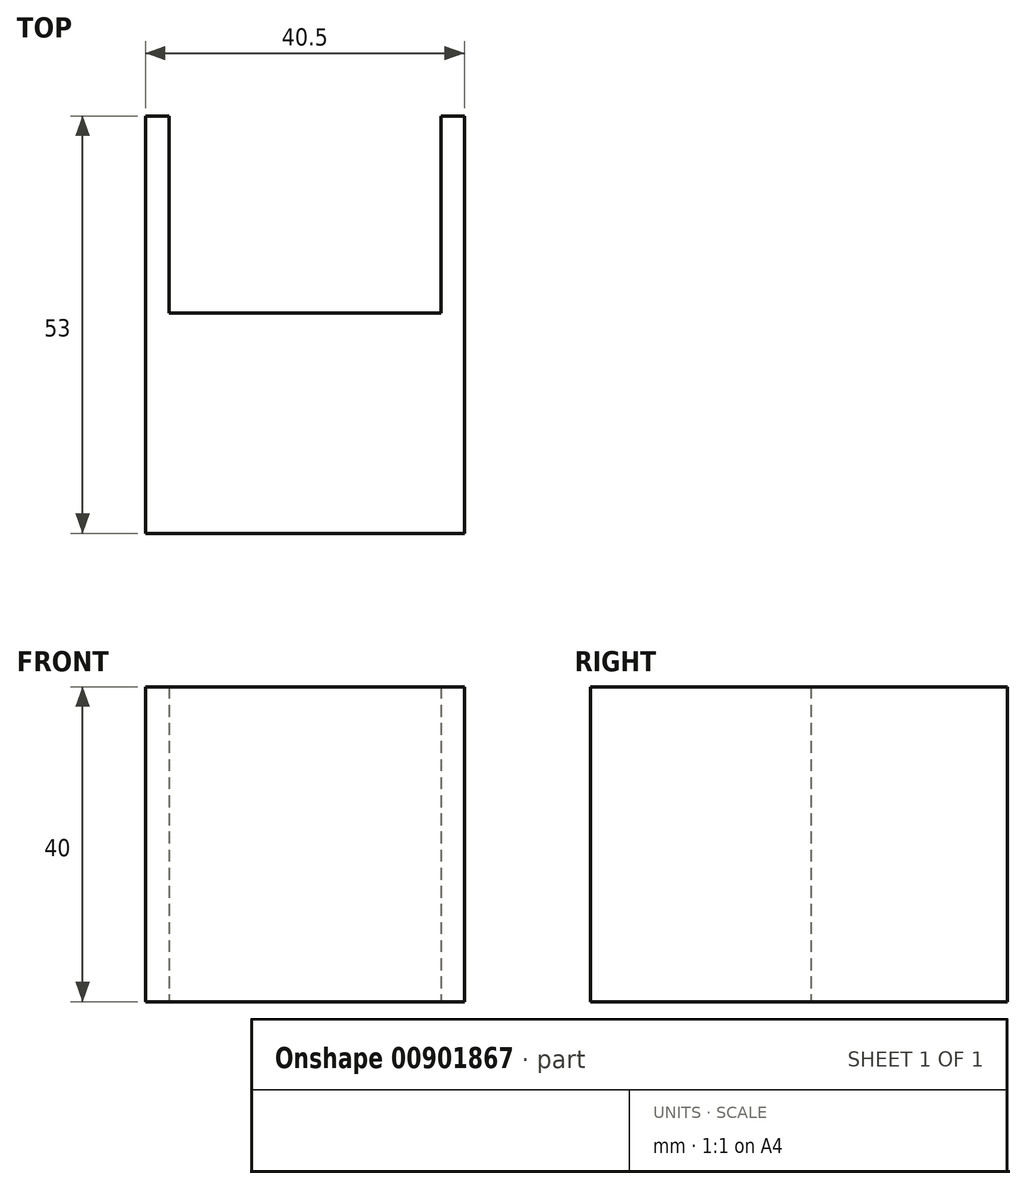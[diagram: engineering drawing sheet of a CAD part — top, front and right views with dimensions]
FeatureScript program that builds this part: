
annotation { "Feature Type Name" : "Feature", "Feature Type Description" : "" }
export const myFeature = defineFeature(function(context is Context, id is Id, definition is map)
    precondition{}
    {
        {
            var Q0;
            Q0=qCreatedBy(makeId("Top.planeOp"),FACE);
            var sketch = newSketch(context, id + "F0", { "sketchPlane" : qUnion([Q0])});
            skLineSegment(sketch, "E0.bottom", {"start": v(-41.97, 18.92) * mm, "end": v(-1.47, 18.92) * mm});
            skLineSegment(sketch, "E0.top", {"start": v(-41.97, -9.08) * mm, "end": v(-1.47, -9.08) * mm});
            skLineSegment(sketch, "E0.left", {"start": v(-41.97, 18.92) * mm, "end": v(-41.97, -9.08) * mm});
            skLineSegment(sketch, "E0.right", {"start": v(-1.47, 18.92) * mm, "end": v(-1.47, -9.08) * mm});
            skLineSegment(sketch, "E1.bottom", {"start": v(-1.47, 18.92) * mm, "end": v(-4.47, 18.92) * mm});
            skLineSegment(sketch, "E1.top", {"start": v(-1.47, 43.92) * mm, "end": v(-4.47, 43.92) * mm});
            skLineSegment(sketch, "E1.left", {"start": v(-1.47, 18.92) * mm, "end": v(-1.47, 43.92) * mm});
            skLineSegment(sketch, "E1.right", {"start": v(-4.47, 18.92) * mm, "end": v(-4.47, 43.92) * mm});
            skLineSegment(sketch, "E2.bottom", {"start": v(-41.97, 18.92) * mm, "end": v(-38.97, 18.92) * mm});
            skLineSegment(sketch, "E2.top", {"start": v(-41.97, 43.92) * mm, "end": v(-38.97, 43.92) * mm});
            skLineSegment(sketch, "E2.left", {"start": v(-41.97, 18.92) * mm, "end": v(-41.97, 43.92) * mm});
            skLineSegment(sketch, "E2.right", {"start": v(-38.97, 18.92) * mm, "end": v(-38.97, 43.92) * mm});
            skSolve(sketch);
        }
        {
            var Q0;
            Q0 = qSketchRegion(id + "F0", true);
            extrude(context, id + "F1", {"entities" : qUnion([Q0]), "depth" : 40 * mm, "offsetDistance" : 25 * mm});
        }
    });
